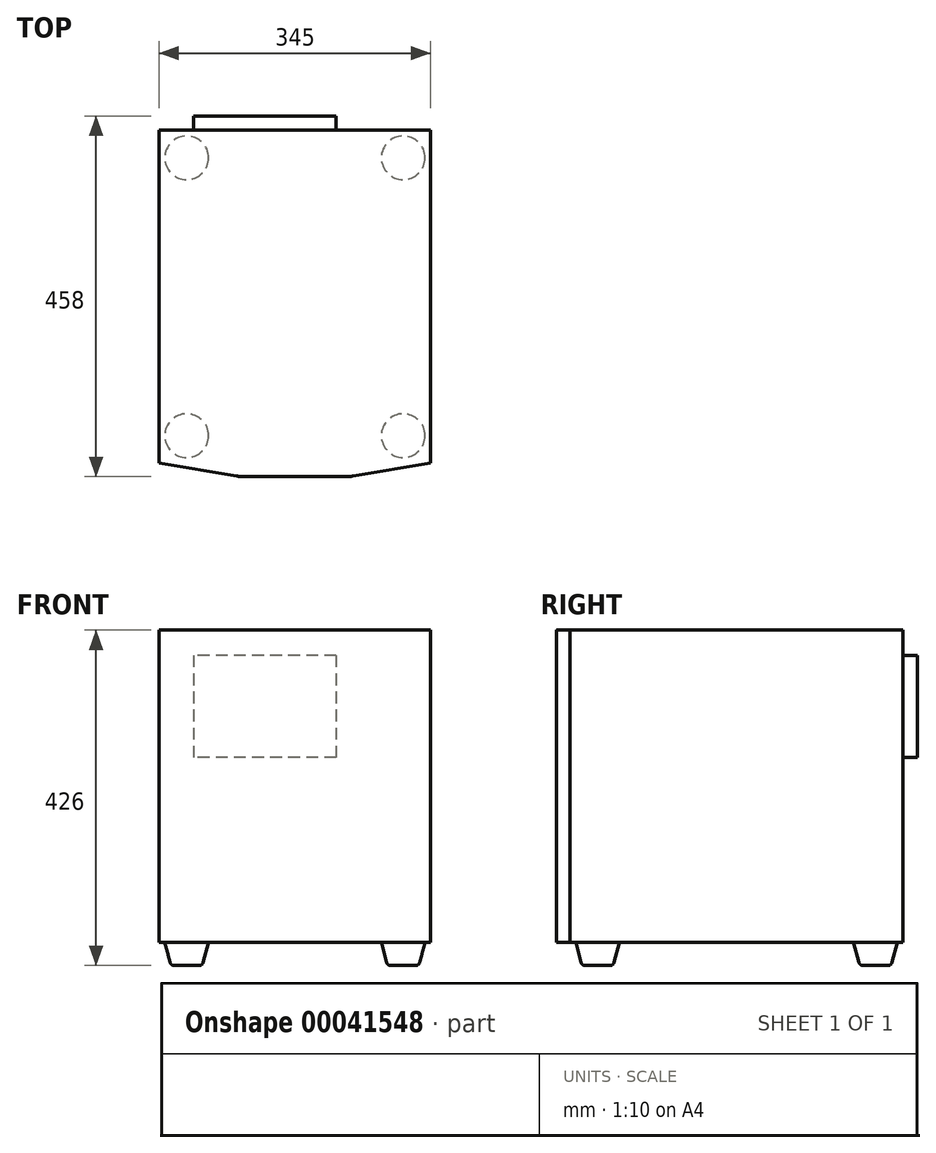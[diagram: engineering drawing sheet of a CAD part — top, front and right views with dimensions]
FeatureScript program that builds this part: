
annotation { "Feature Type Name" : "Feature", "Feature Type Description" : "" }
export const myFeature = defineFeature(function(context is Context, id is Id, definition is map)
    precondition{}
    {
        {
            var Q0;
            Q0=qCreatedBy(makeId("Top.planeOp"),FACE);
            cPlane(context, id + "F0", {"entities" : qUnion([Q0]), "cplaneType" : CPlaneType.OFFSET, "offset" : 426 * mm, "width" : 150 * mm, "height" : 150 * mm});
        }
        {
            var Q0;
            Q0=qCreatedBy(id+"F0.planeOp",FACE);
            cPlane(context, id + "F1", {"entities" : qUnion([Q0]), "cplaneType" : CPlaneType.OFFSET, "offset" : 397 * mm, "oppositeDirection" : true, "width" : 150 * mm, "height" : 150 * mm});
        }
        {
            var Q0;
            Q0=qCreatedBy(id+"F0.planeOp",FACE);
            var sketch = newSketch(context, id + "F2", { "sketchPlane" : qUnion([Q0])});
            skLineSegment(sketch, "E0.bottom", {"start": v(-172.5, 211.5) * mm, "end": v(172.5, 211.5) * mm});
            skLineSegment(sketch, "E0.left", {"start": v(-172.5, 211.5) * mm, "end": v(-172.5, -211.5) * mm});
            skLineSegment(sketch, "E0.right", {"start": v(172.5, 211.5) * mm, "end": v(172.5, -211.5) * mm});
            skLineSegment(sketch, "E1", {"start": v(-172.5, 0) * mm, "end": v(0, 0) * mm, "construction": true});
            skLineSegment(sketch, "E2", {"start": v(0, 0) * mm, "end": v(0, -228.5) * mm, "construction": true});
            skLineSegment(sketch, "E3", {"start": v(-172.5, -211.5) * mm, "end": v(-70, -228.5) * mm});
            skLineSegment(sketch, "E4", {"start": v(-70, -228.5) * mm, "end": v(70, -228.5) * mm});
            skLineSegment(sketch, "E5", {"start": v(70, -228.5) * mm, "end": v(172.5, -211.5) * mm});
            skSolve(sketch);
        }
        {
            var Q0;
            Q0=makeQuery(id+"F2.imprint","IMPRINT",FACE,{"disambiguationData":[TD([[makeQuery(id+"F2.imprint","IMPRINT",EDGE,{"derivedFrom":sQuery(id+"F2.wireOp",EDGE,"E0.bottom")}),-1.0]])]});
            var Q1;
            Q1=qCreatedBy(id+"F1.planeOp",FACE);
            extrude(context, id + "F3", {"entities" : qUnion([Q0]), "endBound" : BoundingType.UP_TO_SURFACE, "oppositeDirection" : true, "endBoundEntityFace" : qUnion([Q1]), "depth" : 25 * mm});
        }
        {
            var Q0;
            Q0=makeQuery(id+"F3.opExtrude","SWEPT_EDGE",EDGE,{"disambiguationData":[OSD([sQuery(id+"F2.wireOp",EDGE,"E3"),sQuery(id+"F2.wireOp",EDGE,"E4")])]});
            var Q1;
            Q1=makeQuery(id+"F3.opExtrude","SWEPT_EDGE",EDGE,{"disambiguationData":[OSD([sQuery(id+"F2.wireOp",EDGE,"E4"),sQuery(id+"F2.wireOp",EDGE,"E5")])]});
            fillet(context, id + "F4", {"entities" : qUnion([Q0, Q1]), "radius" : 50 * mm, "tangentPropagation" : true, "allowEdgeOverflow" : false});
        }
        {
            var Q0;
            Q0=qCreatedBy(id+"F1.planeOp",FACE);
            var sketch = newSketch(context, id + "F5", { "sketchPlane" : qUnion([Q0])});
            skLineSegment(sketch, "E6.bottom", {"start": v(-137.5, 176.5) * mm, "end": v(137.5, 176.5) * mm, "construction": true});
            skLineSegment(sketch, "E6.top", {"start": v(-137.5, -176.5) * mm, "end": v(137.5, -176.5) * mm, "construction": true});
            skLineSegment(sketch, "E6.left", {"start": v(-137.5, 176.5) * mm, "end": v(-137.5, -176.5) * mm, "construction": true});
            skLineSegment(sketch, "E6.right", {"start": v(137.5, 176.5) * mm, "end": v(137.5, -176.5) * mm, "construction": true});
            skLineSegment(sketch, "E7", {"start": v(-137.5, 0) * mm, "end": v(0, 0) * mm, "construction": true});
            skPoint(sketch, "E7.endSnap0", {"position": v(-137.5, 0) * mm});
            skLineSegment(sketch, "E8", {"start": v(0, 0) * mm, "end": v(0, 176.5) * mm, "construction": true});
            skPoint(sketch, "E9", {"position": v(137.5, 176.5) * mm});
            skPoint(sketch, "E10", {"position": v(-137.5, 176.5) * mm});
            skPoint(sketch, "E11", {"position": v(-137.5, -176.5) * mm});
            skPoint(sketch, "E12", {"position": v(137.5, -176.5) * mm});
            skSolve(sketch);
        }
        {
            var Q0;
            Q0=sQuery(id+"F5.wireOp",VERTEX,"E10");
            var Q1;
            Q1=qCreatedBy(makeId("Front.planeOp"),FACE);
            cPlane(context, id + "F6", {"entities" : qUnion([Q0, Q1]), "cplaneType" : CPlaneType.PLANE_POINT, "offset" : 150 * mm, "width" : 150 * mm, "height" : 150 * mm});
        }
        {
            var Q0;
            Q0=qCreatedBy(id+"F6.planeOp",FACE);
            var sketch = newSketch(context, id + "F7", { "sketchPlane" : qUnion([Q0])});
            skLineSegment(sketch, "E13", {"start": v(-109.73, 29) * mm, "end": v(-116.5, 3.7) * mm});
            skLineSegment(sketch, "E14", {"start": v(-121.34, 0) * mm, "end": v(-137.5, 0) * mm});
            skLineSegment(sketch, "E15", {"start": v(-137.5, 0) * mm, "end": v(-137.5, 29) * mm});
            skLineSegment(sketch, "E16", {"start": v(-137.5, 29) * mm, "end": v(-109.73, 29) * mm});
            skPoint(sketch, "E17.visualSharp", {"position": v(-117.5, 0) * mm});
            skArc(sketch, "E17.filletArc", {"start": v(-121.34, 0) * mm, "mid": v(-118.3, 1.03) * mm, "end": v(-116.5, 3.7) * mm});
            skSolve(sketch);
        }
        {
            var Q0;
            Q0=makeQuery(id+"F7.imprint","IMPRINT",FACE,{"disambiguationData":[TD([[makeQuery(id+"F7.imprint","IMPRINT",EDGE,{"derivedFrom":sQuery(id+"F7.wireOp",EDGE,"E13")}),-1.0]])]});
            var Q1;
            Q1=sQuery(id+"F7.wireOp",EDGE,"E15");
            revolve(context, id + "F8", {"entities" : qUnion([Q0]), "axis" : qUnion([Q1]), "revolveType" : RevolveType.FULL});
        }
        {
            var Q0;
            Q0=makeQuery(id+"F8.opRevolve","SWEPT_BODY",BODY,{"disambiguationData":[OSD([sQuery(id+"F7.wireOp",EDGE,"E13"),sQuery(id+"F7.wireOp",EDGE,"E14"),sQuery(id+"F7.wireOp",EDGE,"E15"),sQuery(id+"F7.wireOp",EDGE,"E16"),sQuery(id+"F7.wireOp",EDGE,"E17.filletArc")])]});
            var Q1;
            Q1=qCreatedBy(makeId("Right.planeOp"),FACE);
            mirror(context, id + "F9", {"entities" : qUnion([Q0]), "mirrorPlane" : qUnion([Q1])});
        }
        {
            var Q0;
            Q0=makeQuery(id+"F8.opRevolve","SWEPT_BODY",BODY,{"disambiguationData":[OSD([sQuery(id+"F7.wireOp",EDGE,"E13"),sQuery(id+"F7.wireOp",EDGE,"E14"),sQuery(id+"F7.wireOp",EDGE,"E15"),sQuery(id+"F7.wireOp",EDGE,"E16"),sQuery(id+"F7.wireOp",EDGE,"E17.filletArc")])]});
            var Q1;
            Q1=makeQuery(id+"F9.opPattern","COPY",BODY,{"derivedFrom":makeQuery(id+"F8.opRevolve","SWEPT_BODY",BODY,{"disambiguationData":[OSD([sQuery(id+"F7.wireOp",EDGE,"E13"),sQuery(id+"F7.wireOp",EDGE,"E14"),sQuery(id+"F7.wireOp",EDGE,"E15"),sQuery(id+"F7.wireOp",EDGE,"E16"),sQuery(id+"F7.wireOp",EDGE,"E17.filletArc")])]}),"instanceName":"1"});
            var Q2;
            Q2=qCreatedBy(makeId("Front.planeOp"),FACE);
            mirror(context, id + "F10", {"entities" : qUnion([Q0, Q1]), "mirrorPlane" : qUnion([Q2])});
        }
        {
            var Q0;
            Q0=makeQuery(id+"F3.opExtrude","SWEPT_FACE",FACE,{"disambiguationData":[OSD([sQuery(id+"F2.wireOp",EDGE,"E0.bottom")])]});
            var sketch = newSketch(context, id + "F11", { "sketchPlane" : qUnion([Q0])});
            skLineSegment(sketch, "E18.bottom", {"start": v(-52.5, 394) * mm, "end": v(128.5, 394) * mm});
            skLineSegment(sketch, "E18.top", {"start": v(-52.5, 264) * mm, "end": v(128.5, 264) * mm});
            skLineSegment(sketch, "E18.left", {"start": v(-52.5, 394) * mm, "end": v(-52.5, 264) * mm});
            skLineSegment(sketch, "E18.right", {"start": v(128.5, 394) * mm, "end": v(128.5, 264) * mm});
            skSolve(sketch);
        }
        {
            var Q0;
            Q0=makeQuery(id+"F11.imprint","IMPRINT",FACE,{"disambiguationData":[TD([[makeQuery(id+"F11.imprint","IMPRINT",EDGE,{"derivedFrom":sQuery(id+"F11.wireOp",EDGE,"E18.bottom")}),-1.0]])]});
            extrude(context, id + "F12", {"entities" : qUnion([Q0]), "operationType" : NewBodyOperationType.ADD, "depth" : 18 * mm});
        }
    });
